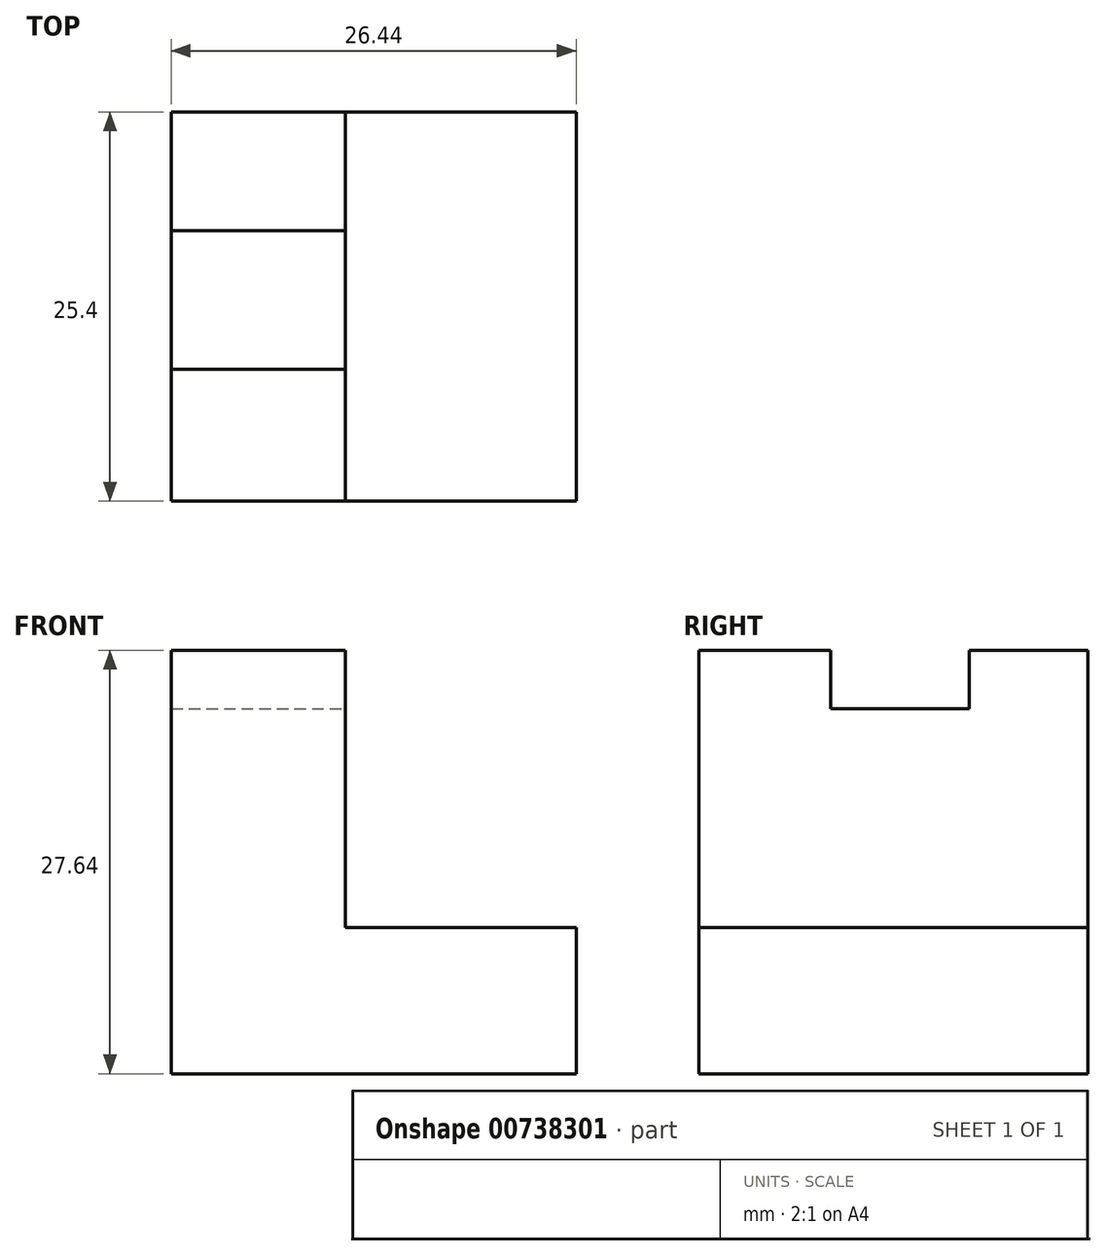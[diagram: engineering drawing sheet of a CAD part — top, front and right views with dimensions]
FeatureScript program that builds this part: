
annotation { "Feature Type Name" : "Feature", "Feature Type Description" : "" }
export const myFeature = defineFeature(function(context is Context, id is Id, definition is map)
    precondition{}
    {
        {
            var Q0;
            Q0=qCreatedBy(makeId("Front.planeOp"),FACE);
            var sketch = newSketch(context, id + "F0", { "sketchPlane" : qUnion([Q0])});
            skLineSegment(sketch, "E0", {"start": v(0, 0) * mm, "end": v(26.44, 0) * mm});
            skLineSegment(sketch, "E1", {"start": v(26.44, 0) * mm, "end": v(26.44, 9.55) * mm});
            skLineSegment(sketch, "E2", {"start": v(26.44, 9.55) * mm, "end": v(11.36, 9.55) * mm});
            skLineSegment(sketch, "E3", {"start": v(11.36, 9.55) * mm, "end": v(11.36, 27.64) * mm});
            skLineSegment(sketch, "E4", {"start": v(11.36, 27.64) * mm, "end": v(0, 27.64) * mm});
            skLineSegment(sketch, "E5", {"start": v(0, 27.64) * mm, "end": v(0, 0) * mm});
            skSolve(sketch);
        }
        {
            var Q0;
            Q0 = qSketchRegion(id + "F0", true);
            extrude(context, id + "F1", {"entities" : qUnion([Q0]), "depth" : 25.4 * mm, "offsetDistance" : 25.4 * mm});
        }
        {
            var Q0;
            Q0=makeQuery(id+"F1.opExtrude","SWEPT_FACE",FACE,{"disambiguationData":[OSD([sQuery(id+"F0.wireOp",EDGE,"E3")])]});
            var sketch = newSketch(context, id + "F2", { "sketchPlane" : qUnion([Q0])});
            skLineSegment(sketch, "E6", {"start": v(-16.79, 27.64) * mm, "end": v(-16.79, 23.82) * mm});
            skLineSegment(sketch, "E7", {"start": v(-16.79, 23.82) * mm, "end": v(-7.74, 23.82) * mm});
            skLineSegment(sketch, "E8", {"start": v(-7.74, 23.82) * mm, "end": v(-7.74, 27.64) * mm});
            skSolve(sketch);
        }
        {
            var Q0;
            {var subQ0=sQuery(id+"F2.wireOp",EDGE,"E6");Q0=makeQuery(id+"F2.imprint","IMPRINT",FACE,{"disambiguationData":[TD([[makeQuery(id+"F2.imprint","IMPRINT",EDGE,{"derivedFrom":subQ0}),1.0]])]});}
            extrude(context, id + "F3", {"entities" : qUnion([Q0]), "operationType" : NewBodyOperationType.REMOVE, "oppositeDirection" : true, "depth" : 25.4 * mm, "offsetDistance" : 25.4 * mm});
        }
    });
